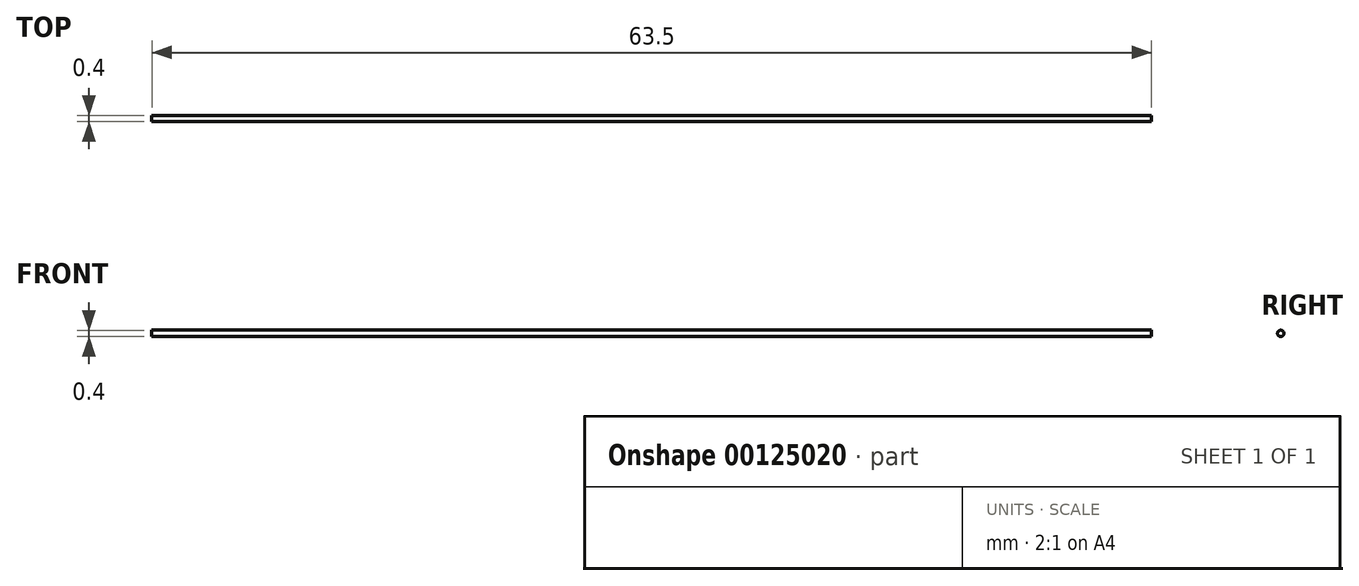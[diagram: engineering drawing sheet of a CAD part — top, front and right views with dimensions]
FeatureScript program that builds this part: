
annotation { "Feature Type Name" : "Feature", "Feature Type Description" : "" }
export const myFeature = defineFeature(function(context is Context, id is Id, definition is map)
    precondition{}
    {
        {
            var Q0;
            Q0=qCreatedBy(makeId("Front.planeOp"),FACE);
            var sketch = newSketch(context, id + "F0", { "sketchPlane" : qUnion([Q0])});
            skLineSegment(sketch, "E0", {"start": v(-29.58, 3.3) * mm, "end": v(33.92, 3.3) * mm});
            skLineSegment(sketch, "E1", {"start": v(33.92, 3.3) * mm, "end": v(33.92, 0) * mm});
            skLineSegment(sketch, "E2", {"start": v(33.92, 0) * mm, "end": v(-29.58, 0) * mm});
            skLineSegment(sketch, "E3", {"start": v(-29.58, 0) * mm, "end": v(-29.58, 3.3) * mm});
            skSolve(sketch);
        }
        {
            var Q0;
            Q0=qCreatedBy(makeId("Right.planeOp"),FACE);
            var sketch = newSketch(context, id + "F1", { "sketchPlane" : qUnion([Q0])});
            skCircle(sketch, "E4", {"center": v(0, 0) * mm, "radius": 0.2 * mm});
            skSolve(sketch);
        }
        {
            var Q0;
            Q0=makeQuery(id+"F1.imprint","IMPRINT",FACE,{"disambiguationData":[TD([[makeQuery(id+"F1.imprint","IMPRINT",EDGE,{"derivedFrom":sQuery(id+"F1.wireOp",EDGE,"E4")}),1.0]])]});
            var Q1;
            Q1=sQuery(id+"F0.wireOp",EDGE,"E0");
            sweep(context, id + "F2", {"profiles" : qUnion([Q0]), "path" : qUnion([Q1])});
        }
    });
